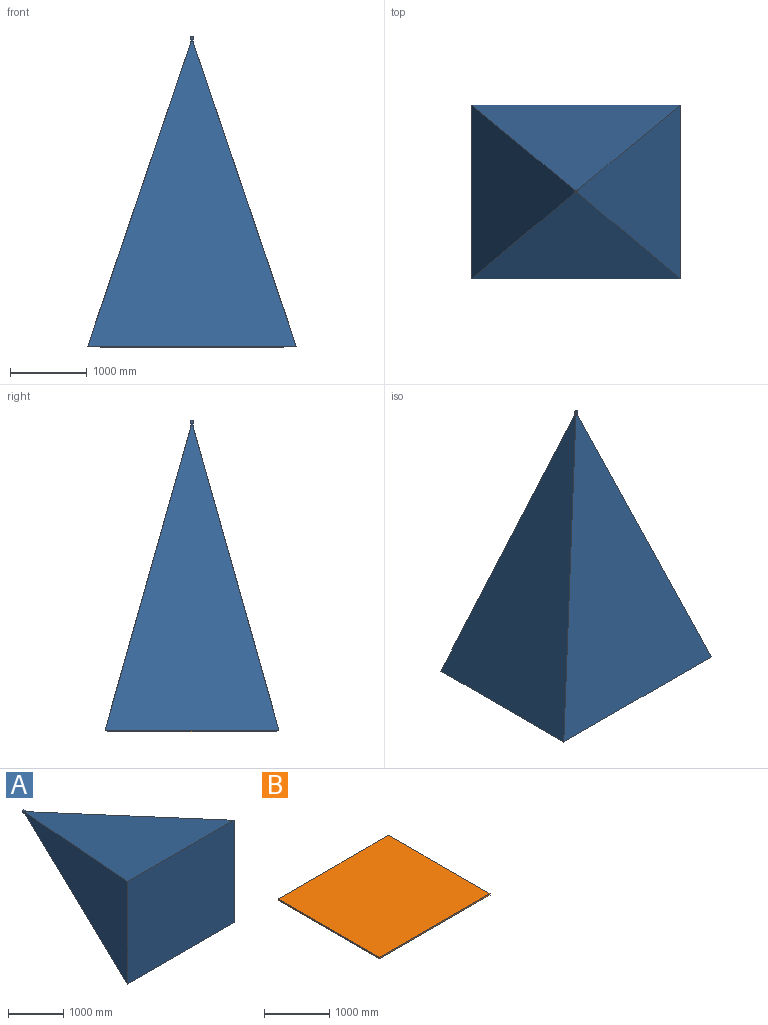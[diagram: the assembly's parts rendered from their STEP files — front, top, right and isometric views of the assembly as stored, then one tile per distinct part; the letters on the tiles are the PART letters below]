
ASSEMBLY  parts=2 mates=1
PART A: 24 faces, bbox 2720x4045x2268.8 mm
  f0: plane 40x30mm, normal (1,0,0), area 1200mm2, adj f1,f3,f4,f5
  f1: plane 40x40mm, normal (0,0,1), area 1600mm2, adj f0,f2,f4,f5
  f2: plane 40x30mm, normal (-1,0,0), area 1200mm2, adj f1,f3,f4,f5
  f3: plane 40x40mm, normal (0,0,-1), area 1600mm2, adj f0,f2,f4,f5
  f4: plane 40x30mm, normal (0,-1,0), area 517.4mm2, adj f0,f1,f2,f3,f10
  f5: plane 40x30mm, normal (0,1,0), area 1121.5mm2, adj f0,f1,f2,f3,f6
  f6: sphere r=5mm, area 157.1mm2, adj f5
  f7: plane 20.46x4.13mm, normal (0,-1,0), area 58.1mm2, adj f10,f16
  f8: plane 14.88x2.02mm, normal (0,-1,0), area 20.3mm2, adj f10,f15
  f9: plane 20.46x4.13mm, normal (0,-1,0), area 58.1mm2, adj f10,f14
  f10: cylinder r=14.74mm len=29.48mm, axis (0,1,0), area 2282.9mm2, adj f4,f7,f8,f9,f11,f13,f14,f15
  f11: plane 14.88x2.02mm, normal (0,-1,0), area 20.3mm2, adj f10,f13
  f12: plane 2720x2268.8mm, normal (0,-1,0), area 6171136mm2, adj f13,f14,f15,f16
  f13: plane 3979.14x2268.8mm, normal (0.95,0.32,0), area 4805764.6mm2, adj f10,f11,f12,f14,f16
  f14: plane 3979.14x2720mm, normal (0,0.27,-0.96), area 5670458.9mm2, adj f9,f10,f12,f13,f15
  f15: plane 3979.14x2268.8mm, normal (-0.95,0.32,0), area 4805764.6mm2, adj f8,f10,f12,f14,f16
  f16: plane 3979.14x2720mm, normal (0,0.27,0.96), area 5670458.9mm2, adj f7,f10,f12,f13,f15
  f17: cylinder r=14.5mm len=29mm, axis (0,-1,0), area 273.3mm2, adj f18,f23
  f18: plane 29x29mm, normal (0,-1,0), area 600.3mm2, adj f17,f19,f20,f21,f22
  f19: plane 7.09x3mm, normal (1,0,0), area 21.3mm2, adj f18,f20,f22,f23
  f20: plane 8.5x3mm, normal (0,0,-1), area 25.5mm2, adj f18,f19,f21,f23
  f21: plane 7.09x3mm, normal (-1,0,0), area 21.3mm2, adj f18,f20,f22,f23
  f22: plane 8.5x3mm, normal (0,0,1), area 25.5mm2, adj f18,f19,f21,f23
  f23: plane 29x29mm, normal (0,1,0), area 600.3mm2, adj f17,f19,f20,f21,f22
PART B: 6 faces, bbox 2400x2200x25 mm
  f0: plane 2200x25mm, normal (1,0,0), area 55000mm2, adj f1,f3,f4,f5
  f1: plane 2400x25mm, normal (0,1,0), area 60000mm2, adj f0,f2,f4,f5
  f2: plane 2200x25mm, normal (-1,0,0), area 55000mm2, adj f1,f3,f4,f5
  f3: plane 2400x25mm, normal (0,-1,0), area 60000mm2, adj f0,f2,f4,f5
  f4: plane 2400x2200mm, normal (0,0,1), area 5280000mm2, adj f0,f1,f2,f3
  f5: plane 2400x2200mm, normal (0,0,-1), area 5280000mm2, adj f0,f1,f2,f3
PLACE A rot(axis=(1,0,0),90deg) t=(5.4,-1.69,4045.28)mm
PLACE B t=(5.4,-1.69,-19.72)mm fixed
MATE parallel A.f17 <-> B.f4  axis (0,0,-1) through (5.4,-1.69,5.28)mm
